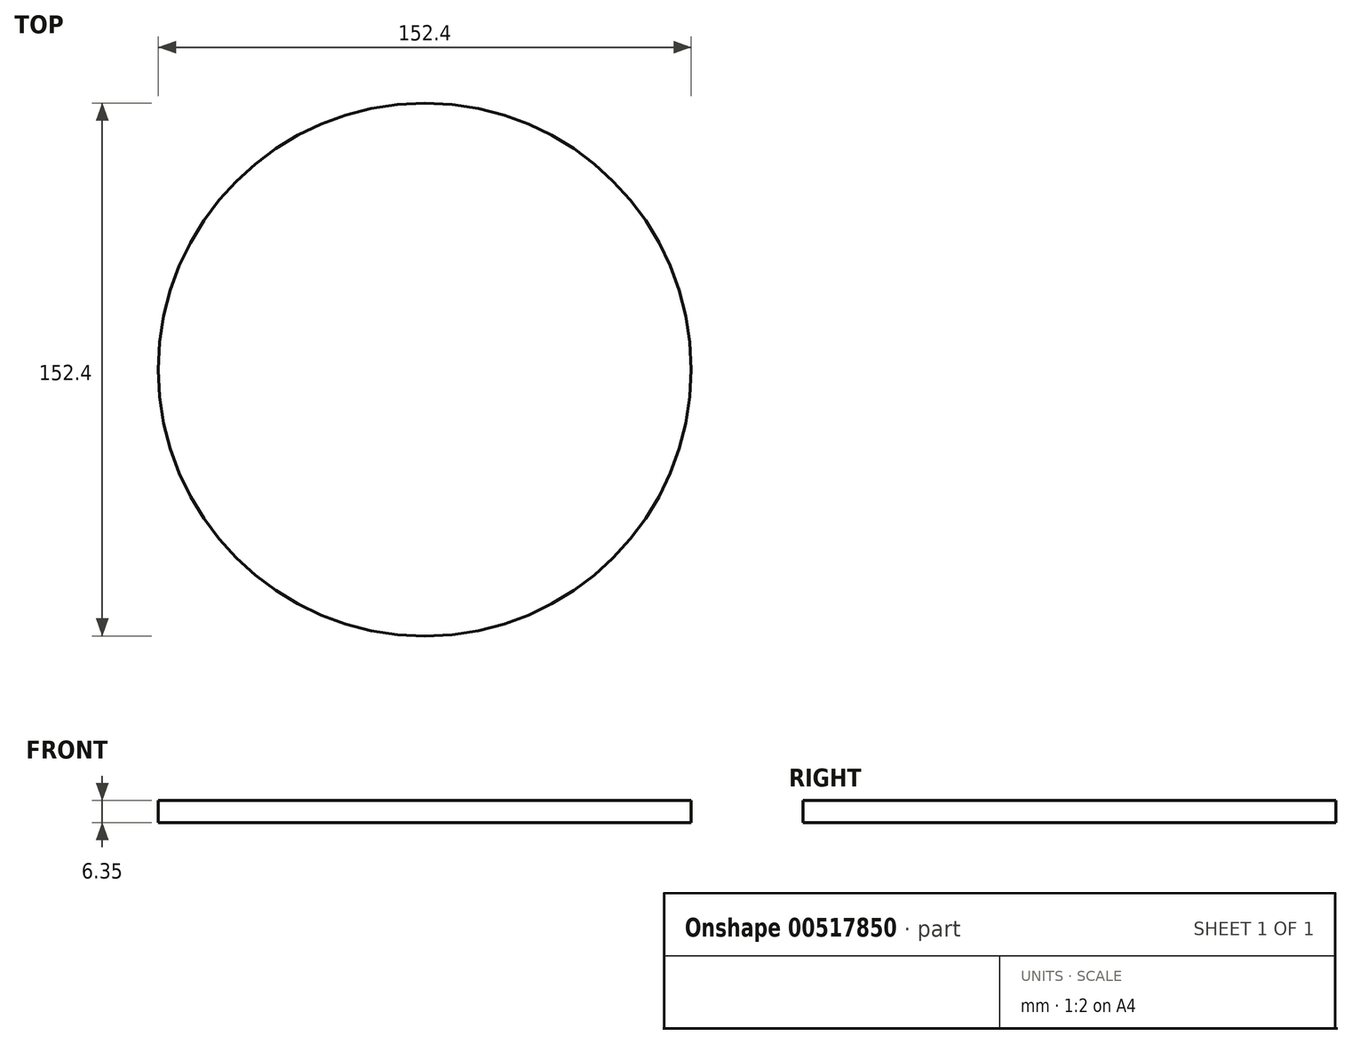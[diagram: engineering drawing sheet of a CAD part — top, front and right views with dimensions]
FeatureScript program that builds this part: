
annotation { "Feature Type Name" : "Feature", "Feature Type Description" : "" }
export const myFeature = defineFeature(function(context is Context, id is Id, definition is map)
    precondition{}
    {
        {
            var Q0;
            Q0=qCreatedBy(makeId("Top.planeOp"),FACE);
            var sketch = newSketch(context, id + "F0", { "sketchPlane" : qUnion([Q0])});
            skCircle(sketch, "E0", {"center": v(0, 0) * mm, "radius": 76.2 * mm});
            skSolve(sketch);
        }
        {
            var Q0;
            Q0=makeQuery(id+"F0.imprint","IMPRINT",FACE,{"disambiguationData":[TD([[makeQuery(id+"F0.imprint","IMPRINT",EDGE,{"derivedFrom":sQuery(id+"F0.wireOp",EDGE,"E0")}),1.0]])]});
            extrude(context, id + "F1", {"entities" : qUnion([Q0]), "depth" : 6.35 * mm, "offsetDistance" : 25.4 * mm});
        }
    });
